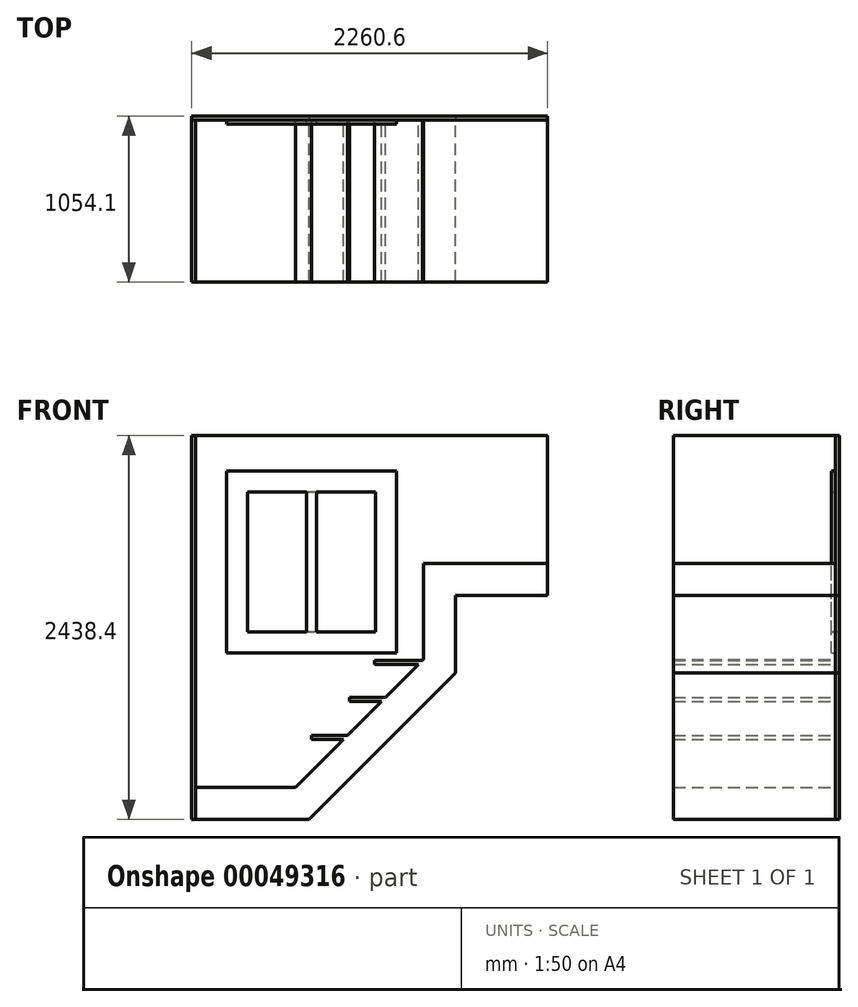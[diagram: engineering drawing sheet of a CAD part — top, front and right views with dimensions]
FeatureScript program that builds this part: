
annotation { "Feature Type Name" : "Feature", "Feature Type Description" : "" }
export const myFeature = defineFeature(function(context is Context, id is Id, definition is map)
    precondition{}
    {
        {
            var Q0;
            Q0=qCreatedBy(makeId("Front.planeOp"),FACE);
            var sketch = newSketch(context, id + "F0", { "sketchPlane" : qUnion([Q0])});
            skLineSegment(sketch, "E0.top", {"start": v(2235.2, 1625.6) * mm, "end": v(1447.8, 1625.6) * mm});
            skLineSegment(sketch, "E0.right", {"start": v(1447.8, 1016) * mm, "end": v(1447.8, 1625.6) * mm});
            skLineSegment(sketch, "E1", {"start": v(1447.8, 1016) * mm, "end": v(1441.45, 1009.65) * mm});
            skLineSegment(sketch, "E2", {"start": v(0, 203.2) * mm, "end": v(635, 203.2) * mm});
            skLineSegment(sketch, "E3", {"start": v(0, 203.2) * mm, "end": v(0, 0) * mm});
            skLineSegment(sketch, "E4", {"start": v(0, 0) * mm, "end": v(719.17, 0) * mm});
            skLineSegment(sketch, "E5.0", {"start": v(1651, 931.83) * mm, "end": v(719.17, 0) * mm});
            skLineSegment(sketch, "E5.1", {"start": v(1651, 931.83) * mm, "end": v(1651, 1422.4) * mm});
            skLineSegment(sketch, "E5.2", {"start": v(2235.2, 1422.4) * mm, "end": v(1651, 1422.4) * mm});
            skLineSegment(sketch, "E6", {"start": v(2235.2, 1625.6) * mm, "end": v(2235.2, 1422.4) * mm});
            skPoint(sketch, "E7.orphan", {"position": v(1005.6, 0) * mm});
            skLineSegment(sketch, "E8", {"start": v(965.2, 533.4) * mm, "end": v(736.6, 533.4) * mm});
            skLineSegment(sketch, "E9", {"start": v(736.6, 508) * mm, "end": v(736.6, 533.4) * mm});
            skLineSegment(sketch, "E10", {"start": v(736.6, 508) * mm, "end": v(939.8, 508) * mm});
            skLineSegment(sketch, "E11", {"start": v(1181.1, 749.3) * mm, "end": v(977.9, 749.3) * mm});
            skLineSegment(sketch, "E12", {"start": v(977.9, 774.7) * mm, "end": v(1206.5, 774.7) * mm});
            skLineSegment(sketch, "E13", {"start": v(977.9, 774.7) * mm, "end": v(977.9, 749.3) * mm});
            skLineSegment(sketch, "E14", {"start": v(1136.65, 1009.65) * mm, "end": v(1441.45, 1009.65) * mm});
            skLineSegment(sketch, "E15", {"start": v(1416.05, 984.25) * mm, "end": v(1136.65, 984.25) * mm});
            skLineSegment(sketch, "E16", {"start": v(1136.65, 1009.65) * mm, "end": v(1136.65, 984.25) * mm});
            skLineSegment(sketch, "E17.trimOffspring", {"start": v(1416.05, 984.25) * mm, "end": v(1206.5, 774.7) * mm});
            skLineSegment(sketch, "E18.trimOffspring", {"start": v(1181.1, 749.3) * mm, "end": v(965.2, 533.4) * mm});
            skLineSegment(sketch, "E19.trimOffspring", {"start": v(939.8, 508) * mm, "end": v(635, 203.2) * mm});
            skSolve(sketch);
        }
        {
            var Q0;
            Q0=makeQuery(id+"F0.imprint","IMPRINT",FACE,{"disambiguationData":[TD([[makeQuery(id+"F0.imprint","IMPRINT",EDGE,{"derivedFrom":sQuery(id+"F0.wireOp",EDGE,"E0.top")}),1.0]])]});
            extrude(context, id + "F1", {"entities" : qUnion([Q0]), "endBound" : BoundingType.SYMMETRIC, "depth" : 1028.7 * mm});
        }
        {
            var Q0;
            Q0=makeQuery(id+"F1.opExtrude","SWEPT_FACE",FACE,{"disambiguationData":[OSD([sQuery(id+"F0.wireOp",EDGE,"E3")])]});
            var sketch = newSketch(context, id + "F2", { "sketchPlane" : qUnion([Q0])});
            skLineSegment(sketch, "E20.bottom", {"start": v(514.35, 0) * mm, "end": v(-514.35, 0) * mm});
            skLineSegment(sketch, "E20.top", {"start": v(514.35, 2438.4) * mm, "end": v(-514.35, 2438.4) * mm});
            skLineSegment(sketch, "E20.left", {"start": v(514.35, 0) * mm, "end": v(514.35, 2438.4) * mm});
            skLineSegment(sketch, "E20.right", {"start": v(-514.35, 0) * mm, "end": v(-514.35, 2438.4) * mm});
            skSolve(sketch);
        }
        {
            var Q0;
            {var subQ2=sQuery(id+"F2.wireOp",EDGE,"E20.bottom");Q0=makeQuery(id+"F2.imprint","IMPRINT",FACE,{"disambiguationData":[TD([[makeQuery(id+"F2.imprint","IMPRINT",EDGE,{"derivedFrom":subQ2}),-1.0]])]});}
            var Q1;
            {var subQ2=sQuery(id+"F2.wireOp",EDGE,"E20.top");Q1=makeQuery(id+"F2.imprint","IMPRINT",FACE,{"disambiguationData":[TD([[makeQuery(id+"F2.imprint","IMPRINT",EDGE,{"derivedFrom":subQ2}),1.0]])]});}
            extrude(context, id + "F3", {"entities" : qUnion([Q0, Q1]), "depth" : 25.4 * mm});
        }
        {
            var Q0;
            Q0=makeQuery(id+"F1.opExtrude","CAP_FACE",FACE,{"disambiguationData":[OSD([sQuery(id+"F0.wireOp",EDGE,"E0.top"),sQuery(id+"F0.wireOp",EDGE,"E0.right"),sQuery(id+"F0.wireOp",EDGE,"E1"),sQuery(id+"F0.wireOp",EDGE,"E2"),sQuery(id+"F0.wireOp",EDGE,"E3"),sQuery(id+"F0.wireOp",EDGE,"E4"),sQuery(id+"F0.wireOp",EDGE,"E5.0"),sQuery(id+"F0.wireOp",EDGE,"E5.1"),sQuery(id+"F0.wireOp",EDGE,"E5.2"),sQuery(id+"F0.wireOp",EDGE,"E6")])],"isStart":true});
            var sketch = newSketch(context, id + "F4", { "sketchPlane" : qUnion([Q0])});
            skLineSegment(sketch, "E21.0", {"start": v(-2235.2, 1422.4) * mm, "end": v(-1651, 1422.4) * mm});
            skLineSegment(sketch, "E22.0", {"start": v(-1651, 931.83) * mm, "end": v(-1651, 1422.4) * mm});
            skLineSegment(sketch, "E23.0", {"start": v(-1651, 931.83) * mm, "end": v(-719.17, 0) * mm});
            skLineSegment(sketch, "E24.0", {"start": v(25.4, 2438.4) * mm, "end": v(25.4, 0) * mm});
            skLineSegment(sketch, "E25", {"start": v(25.4, 0) * mm, "end": v(-719.17, 0) * mm});
            skLineSegment(sketch, "E26", {"start": v(-2235.2, 1422.4) * mm, "end": v(-2235.2, 2438.4) * mm});
            skLineSegment(sketch, "E27", {"start": v(-2235.2, 2438.4) * mm, "end": v(25.4, 2438.4) * mm});
            skSolve(sketch);
        }
        {
            var Q0;
            {var subQ1=sQuery(id+"F4.wireOp",EDGE,"E24.0");Q0=makeQuery(id+"F4.imprint","IMPRINT",FACE,{"disambiguationData":[TD([[makeQuery(id+"F4.imprint","IMPRINT",EDGE,{"derivedFrom":subQ1}),-1.0]])]});}
            var Q1;
            {var subQ2=sQuery(id+"F4.wireOp",EDGE,"E21.0");Q1=makeQuery(id+"F4.imprint","IMPRINT",FACE,{"disambiguationData":[TD([[makeQuery(id+"F4.imprint","IMPRINT",EDGE,{"derivedFrom":subQ2}),1.0]])]});}
            extrude(context, id + "F5", {"entities" : qUnion([Q0, Q1]), "depth" : 25.4 * mm});
        }
        {
            var Q0;
            Q0=makeQuery(id+"F5.opExtrude","CAP_FACE",FACE,{"disambiguationData":[OSD([sQuery(id+"F4.wireOp",EDGE,"E21.0"),sQuery(id+"F4.wireOp",EDGE,"E22.0"),sQuery(id+"F4.wireOp",EDGE,"E23.0"),sQuery(id+"F4.wireOp",EDGE,"E24.0"),sQuery(id+"F4.wireOp",EDGE,"E25"),sQuery(id+"F4.wireOp",EDGE,"E26"),sQuery(id+"F4.wireOp",EDGE,"E27")])],"isStart":true});
            var sketch = newSketch(context, id + "F6", { "sketchPlane" : qUnion([Q0])});
            skLineSegment(sketch, "E28.bottom", {"start": v(1143, 1189.97) * mm, "end": v(330.2, 1189.97) * mm});
            skLineSegment(sketch, "E28.top", {"start": v(1143, 2078.97) * mm, "end": v(330.2, 2078.97) * mm});
            skLineSegment(sketch, "E28.left", {"start": v(1143, 1189.97) * mm, "end": v(1143, 2078.97) * mm});
            skLineSegment(sketch, "E28.right", {"start": v(330.2, 1189.97) * mm, "end": v(330.2, 2078.97) * mm});
            skSolve(sketch);
        }
        {
            var Q0;
            Q0 = qSketchRegion(id + "F6", true);
            extrude(context, id + "F7", {"entities" : qUnion([Q0]), "operationType" : NewBodyOperationType.REMOVE, "endBound" : BoundingType.THROUGH_ALL, "oppositeDirection" : true, "depth" : 25.4 * mm});
        }
        {
            var Q0;
            Q0=makeQuery(id+"F5.opExtrude","CAP_FACE",FACE,{"disambiguationData":[OSD([sQuery(id+"F4.wireOp",EDGE,"E21.0"),sQuery(id+"F4.wireOp",EDGE,"E22.0"),sQuery(id+"F4.wireOp",EDGE,"E23.0"),sQuery(id+"F4.wireOp",EDGE,"E24.0"),sQuery(id+"F4.wireOp",EDGE,"E25"),sQuery(id+"F4.wireOp",EDGE,"E26"),sQuery(id+"F4.wireOp",EDGE,"E27")])],"isStart":true});
            var sketch = newSketch(context, id + "F8", { "sketchPlane" : qUnion([Q0])});
            skLineSegment(sketch, "E29.0", {"start": v(330.2, 1189.97) * mm, "end": v(330.2, 2078.97) * mm});
            skLineSegment(sketch, "E30.0", {"start": v(1143, 1189.97) * mm, "end": v(330.2, 1189.97) * mm});
            skLineSegment(sketch, "E31.0", {"start": v(1143, 1189.97) * mm, "end": v(1143, 2078.97) * mm});
            skLineSegment(sketch, "E32.0", {"start": v(1143, 2078.97) * mm, "end": v(768.35, 2078.97) * mm});
            skLineSegment(sketch, "E33.0", {"start": v(1276.35, 2212.32) * mm, "end": v(196.85, 2212.32) * mm});
            skLineSegment(sketch, "E33.1", {"start": v(1276.35, 1056.62) * mm, "end": v(1276.35, 2212.32) * mm});
            skLineSegment(sketch, "E33.2", {"start": v(1276.35, 1056.62) * mm, "end": v(196.85, 1056.62) * mm});
            skLineSegment(sketch, "E33.3", {"start": v(196.85, 1056.62) * mm, "end": v(196.85, 2212.32) * mm});
            skLineSegment(sketch, "E34.left", {"start": v(704.85, 2078.97) * mm, "end": v(704.85, 1189.97) * mm});
            skLineSegment(sketch, "E34.right", {"start": v(768.35, 2078.97) * mm, "end": v(768.35, 1189.97) * mm});
            skLineSegment(sketch, "E35.trimOffspring", {"start": v(704.85, 2078.97) * mm, "end": v(330.2, 2078.97) * mm});
            skLineSegment(sketch, "E36.trimOffspring", {"start": v(704.85, 1189.97) * mm, "end": v(330.2, 1189.97) * mm});
            skSolve(sketch);
        }
        {
            var Q0;
            Q0=makeQuery(id+"F8.imprint","IMPRINT",FACE,{"disambiguationData":[TD([[makeQuery(id+"F8.imprint","IMPRINT",EDGE,{"derivedFrom":sQuery(id+"F8.wireOp",EDGE,"E29.0")}),1.0]])]});
            var Q1;
            {var subQ0=sQuery(id+"F8.wireOp",EDGE,"E34.left");Q1=makeQuery(id+"F8.imprint","IMPRINT",FACE,{"disambiguationData":[TD([[makeQuery(id+"F8.imprint","IMPRINT",EDGE,{"derivedFrom":subQ0}),1.0]])]});}
            extrude(context, id + "F9", {"entities" : qUnion([Q0, Q1]), "operationType" : NewBodyOperationType.ADD, "depth" : 25.4 * mm});
        }
    });
